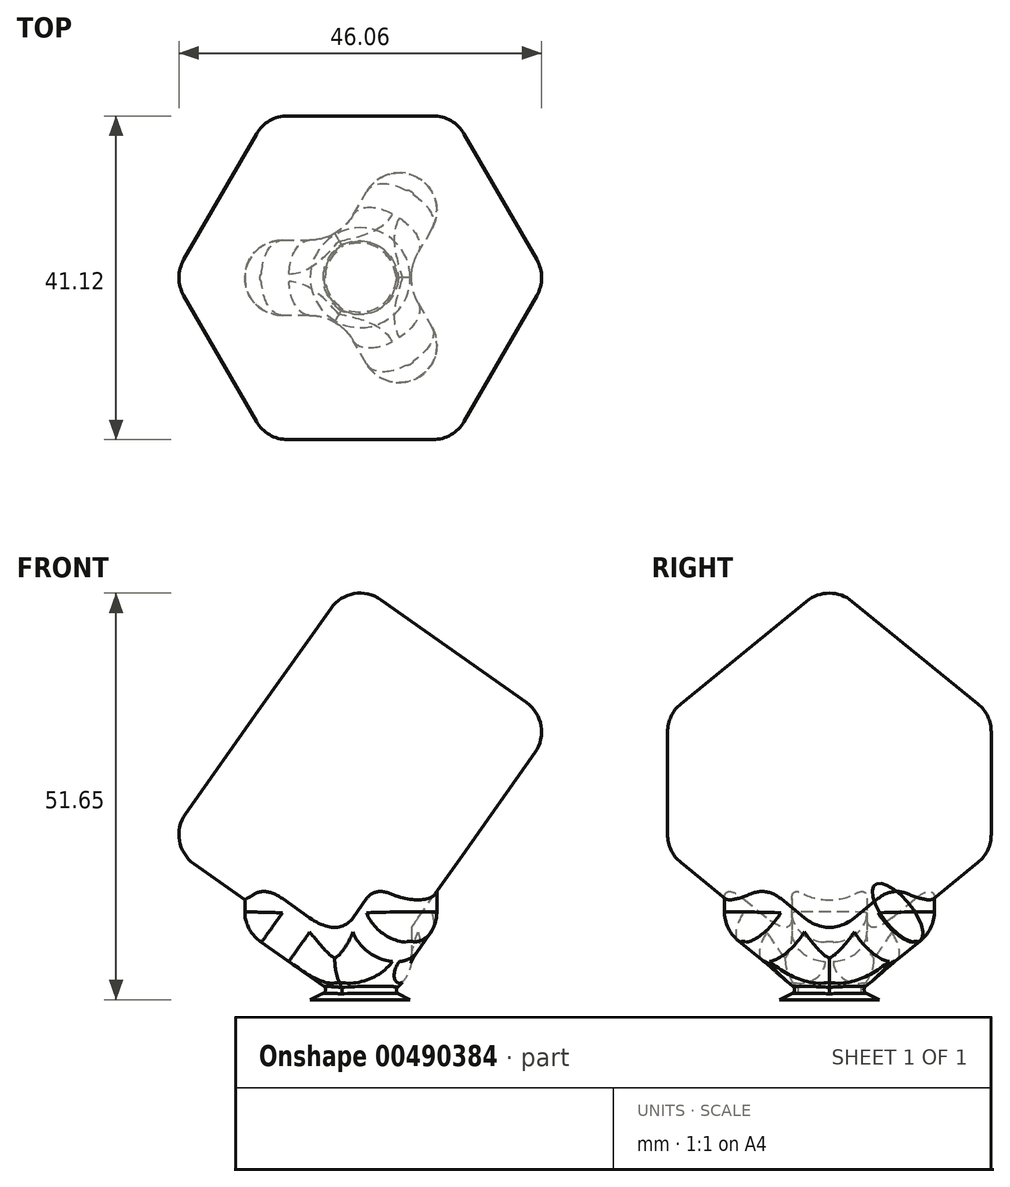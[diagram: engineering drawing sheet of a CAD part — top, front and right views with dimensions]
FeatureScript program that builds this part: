
annotation { "Feature Type Name" : "Feature", "Feature Type Description" : "" }
export const myFeature = defineFeature(function(context is Context, id is Id, definition is map)
    precondition{}
    {
        {
            var Q0;
            Q0=qCreatedBy(makeId("Front.planeOp"),FACE);
            var sketch = newSketch(context, id + "F0", { "sketchPlane" : qUnion([Q0])});
            skLineSegment(sketch, "E0", {"start": v(0, 0) * mm, "end": v(-25.92, 18.33) * mm});
            skLineSegment(sketch, "E1", {"start": v(-25.92, 18.33) * mm, "end": v(0, 55) * mm});
            skLineSegment(sketch, "E2", {"start": v(0, 55) * mm, "end": v(25.92, 36.66) * mm});
            skLineSegment(sketch, "E3", {"start": v(25.92, 36.66) * mm, "end": v(0, 0) * mm});
            skSolve(sketch);
        }
        {
            var Q0;
            Q0=sQuery(id+"F0.wireOp",EDGE,"E3");
            cPlane(context, id + "F1", {"entities" : qUnion([Q0]), "cplaneType" : CPlaneType.LINE_ANGLE, "offset" : 25.4 * mm, "angle" : 0 * degree, "width" : 152.4 * mm, "height" : 152.4 * mm});
        }
        {
            var Q0;
            Q0=qCreatedBy(id+"F1.planeOp",FACE);
            var sketch = newSketch(context, id + "F2", { "sketchPlane" : qUnion([Q0])});
            skLineSegment(sketch, "E4", {"start": v(0, 0) * mm, "end": v(-22.45, 22.45) * mm});
            skLineSegment(sketch, "E5", {"start": v(-22.45, 22.45) * mm, "end": v(0, 44.9) * mm});
            skLineSegment(sketch, "E6", {"start": v(0, 44.9) * mm, "end": v(22.45, 22.45) * mm});
            skLineSegment(sketch, "E7", {"start": v(22.45, 22.45) * mm, "end": v(0, 0) * mm});
            skSolve(sketch);
        }
        {
            var Q0;
            Q0 = qSketchRegion(id + "F2", true);
            extrude(context, id + "F3", {"entities" : qUnion([Q0]), "depth" : 31.75 * mm});
        }
        {
            var Q0;
            Q0=makeQuery(id+"F3.opExtrude","SWEPT_FACE",FACE,{"disambiguationData":[OSD([sQuery(id+"F2.wireOp",EDGE,"E7")])]});
            var Q1;
            Q1=makeQuery(id+"F3.opExtrude","SWEPT_FACE",FACE,{"disambiguationData":[OSD([sQuery(id+"F2.wireOp",EDGE,"E6")])]});
            var Q2;
            Q2=makeQuery(id+"F3.opExtrude","CAP_FACE",FACE,{"disambiguationData":[OSD([sQuery(id+"F2.wireOp",EDGE,"E4"),sQuery(id+"F2.wireOp",EDGE,"E5"),sQuery(id+"F2.wireOp",EDGE,"E6"),sQuery(id+"F2.wireOp",EDGE,"E7")])],"isStart":true});
            var Q3;
            Q3=makeQuery(id+"F3.opExtrude","SWEPT_FACE",FACE,{"disambiguationData":[OSD([sQuery(id+"F2.wireOp",EDGE,"E5")])]});
            var Q4;
            Q4=makeQuery(id+"F3.opExtrude","CAP_FACE",FACE,{"disambiguationData":[OSD([sQuery(id+"F2.wireOp",EDGE,"E4"),sQuery(id+"F2.wireOp",EDGE,"E5"),sQuery(id+"F2.wireOp",EDGE,"E6"),sQuery(id+"F2.wireOp",EDGE,"E7")])],"isStart":false});
            var Q5;
            Q5=makeQuery(id+"F3.opExtrude","SWEPT_FACE",FACE,{"disambiguationData":[OSD([sQuery(id+"F2.wireOp",EDGE,"E4")])]});
            fillet(context, id + "F4", {"entities" : qUnion([Q0, Q1, Q2, Q3, Q4, Q5]), "radius" : 4.57 * mm, "tangentPropagation" : true, "allowEdgeOverflow" : false});
        }
        {
            var Q0;
            Q0=qCreatedBy(makeId("Top.planeOp"),FACE);
            var sketch = newSketch(context, id + "F5", { "sketchPlane" : qUnion([Q0])});
            skLineSegment(sketch, "E8", {"start": v(0, 0) * mm, "end": v(7.33, -12.7) * mm, "construction": true});
            skLineSegment(sketch, "E9", {"start": v(7.33, -12.7) * mm, "end": v(7.33, 12.7) * mm, "construction": true});
            skLineSegment(sketch, "E10", {"start": v(7.33, 12.7) * mm, "end": v(0, 0) * mm, "construction": true});
            skLineSegment(sketch, "E11", {"start": v(9.08, -6.18) * mm, "end": v(7.35, -3.18) * mm, "construction": true});
            skLineSegment(sketch, "E12", {"start": v(7.35, 3.17) * mm, "end": v(9.08, 6.18) * mm, "construction": true});
            skArc(sketch, "E13", {"start": v(7.33, -12.7) * mm, "mid": v(9.56, -9.8) * mm, "end": v(9.08, -6.18) * mm, "construction": true});
            skArc(sketch, "E14", {"start": v(9.08, 6.18) * mm, "mid": v(9.56, 9.8) * mm, "end": v(7.33, 12.7) * mm, "construction": true});
            skArc(sketch, "E15", {"start": v(7.35, 3.17) * mm, "mid": v(6.5, 0) * mm, "end": v(7.35, -3.17) * mm, "construction": true});
            skLineSegment(sketch, "E16", {"start": v(0, 0) * mm, "end": v(12.85, 0) * mm, "construction": true});
            skArc(sketch, "E17.1.0", {"start": v(7.33, 12.7) * mm, "mid": v(3.7, 13.18) * mm, "end": v(0.8, 10.95) * mm, "construction": true});
            skLineSegment(sketch, "E17.1.1", {"start": v(0.8, 10.95) * mm, "end": v(-0.92, 7.95) * mm, "construction": true});
            skArc(sketch, "E17.1.2", {"start": v(-6.42, 4.78) * mm, "mid": v(-4.78, 5) * mm, "end": v(-3.25, 5.63) * mm});
            skLineSegment(sketch, "E17.1.3", {"start": v(-6.42, 4.78) * mm, "end": v(-9.89, 4.78) * mm});
            skArc(sketch, "E17.1.4", {"start": v(-9.89, 4.78) * mm, "mid": v(-13.27, 3.38) * mm, "end": v(-14.66, 0) * mm});
            skArc(sketch, "E17.2.0", {"start": v(-14.66, 0) * mm, "mid": v(-13.27, -3.38) * mm, "end": v(-9.89, -4.78) * mm});
            skLineSegment(sketch, "E17.2.1", {"start": v(-9.89, -4.78) * mm, "end": v(-6.42, -4.78) * mm});
            skArc(sketch, "E17.2.2", {"start": v(-0.92, -7.95) * mm, "mid": v(-1.93, -6.64) * mm, "end": v(-3.25, -5.63) * mm});
            skLineSegment(sketch, "E17.2.3", {"start": v(-0.92, -7.95) * mm, "end": v(0.8, -10.95) * mm, "construction": true});
            skArc(sketch, "E17.2.4", {"start": v(0.8, -10.95) * mm, "mid": v(3.7, -13.18) * mm, "end": v(7.33, -12.7) * mm, "construction": true});
            skPoint(sketch, "E17.center", {"position": v(0, 0) * mm});
            skLineSegment(sketch, "E18", {"start": v(0, 0) * mm, "end": v(-3.25, 5.63) * mm});
            skLineSegment(sketch, "E19", {"start": v(0, 0) * mm, "end": v(-3.25, -5.63) * mm});
            skArc(sketch, "E20", {"start": v(-3.25, 5.63) * mm, "mid": v(-1.93, 6.64) * mm, "end": v(-0.92, 7.95) * mm});
            skArc(sketch, "E21", {"start": v(-3.25, -5.63) * mm, "mid": v(-4.78, -5) * mm, "end": v(-6.42, -4.78) * mm});
            skSolve(sketch);
        }
        {
            var Q0;
            Q0=makeQuery(id+"F5.imprint","IMPRINT",FACE,{"disambiguationData":[TD([[makeQuery(id+"F5.imprint","IMPRINT",EDGE,{"derivedFrom":sQuery(id+"F5.wireOp",EDGE,"E17.1.2")}),-1.0]])]});
            var Q1;
            Q1=makeQuery(id+"F3.opExtrude","SWEPT_BODY",BODY,{"disambiguationData":[OSD([sQuery(id+"F2.wireOp",EDGE,"E4"),sQuery(id+"F2.wireOp",EDGE,"E5"),sQuery(id+"F2.wireOp",EDGE,"E6"),sQuery(id+"F2.wireOp",EDGE,"E7")])]});
            extrude(context, id + "F6", {"entities" : qUnion([Q0]), "endBound" : BoundingType.UP_TO_BODY, "endBoundEntityBody" : qUnion([Q1]), "depth" : 25.4 * mm});
        }
        {
            var Q0;
            Q0=qCreatedBy(id+"F1.planeOp",FACE);
            var sketch = newSketch(context, id + "F7", { "sketchPlane" : qUnion([Q0])});
            skArc(sketch, "E22", {"start": v(-5.63, 1.14) * mm, "mid": v(0, -1.28) * mm, "end": v(5.63, 1.14) * mm});
            skLineSegment(sketch, "E23", {"start": v(15.4, -11.7) * mm, "end": v(-17.38, -11.7) * mm});
            skLineSegment(sketch, "E24", {"start": v(-17.38, 1.14) * mm, "end": v(-17.38, -11.7) * mm});
            skLineSegment(sketch, "E25", {"start": v(15.4, 1.14) * mm, "end": v(15.4, -11.7) * mm});
            skLineSegment(sketch, "E26", {"start": v(-5.63, 1.14) * mm, "end": v(-17.38, 1.14) * mm});
            skLineSegment(sketch, "E27", {"start": v(5.63, 1.14) * mm, "end": v(15.4, 1.14) * mm});
            skSolve(sketch);
        }
        {
            var Q0;
            Q0 = qSketchRegion(id + "F7", true);
            extrude(context, id + "F8", {"entities" : qUnion([Q0]), "operationType" : NewBodyOperationType.REMOVE, "endBound" : BoundingType.THROUGH_ALL, "depth" : 25.4 * mm, "hasSecondDirection" : true, "secondDirectionBound" : SecondDirectionBoundingType.THROUGH_ALL, "secondDirectionOppositeDirection" : true, "secondDirectionDepth" : 25.4 * mm});
        }
        {
            var Q0;
            Q0=makeQuery(id+"F6.opExtrude","SWEPT_BODY",BODY,{"disambiguationData":[OSD([sQuery(id+"F5.wireOp",EDGE,"E17.1.2"),sQuery(id+"F5.wireOp",EDGE,"E17.1.3"),sQuery(id+"F5.wireOp",EDGE,"E17.1.4"),sQuery(id+"F5.wireOp",EDGE,"E17.2.0"),sQuery(id+"F5.wireOp",EDGE,"E17.2.1"),sQuery(id+"F5.wireOp",EDGE,"E18"),sQuery(id+"F5.wireOp",EDGE,"E19"),sQuery(id+"F5.wireOp",EDGE,"E21")])]});
            var Q1;
            Q1=makeQuery(id+"F6.opExtrude","SWEPT_EDGE",EDGE,{"disambiguationData":[OSD([sQuery(id+"F5.wireOp",EDGE,"E18"),sQuery(id+"F5.wireOp",EDGE,"E19")])]});
            circularPattern(context, id + "F9", {"operationType" : NewBodyOperationType.ADD, "entities" : qUnion([Q0]), "axis" : qUnion([Q1]), "angle" : 360 * degree, "instanceCount" : 3, "equalSpace" : true});
        }
        {
            var Q0;
            Q0=qCreatedBy(makeId("Front.planeOp"),FACE);
            var sketch = newSketch(context, id + "F10", { "sketchPlane" : qUnion([Q0])});
            skLineSegment(sketch, "E28", {"start": v(0, 3.18) * mm, "end": v(6.35, 0) * mm});
            skPoint(sketch, "E29.orphan", {"position": v(6.5, 3.7) * mm});
            skLineSegment(sketch, "E30", {"start": v(0, 0) * mm, "end": v(0, 3.18) * mm});
            skLineSegment(sketch, "E31", {"start": v(6.35, 0) * mm, "end": v(0, 0) * mm});
            skSolve(sketch);
        }
        {
            var Q0;
            Q0=makeQuery(id+"F10.imprint","IMPRINT",FACE,{"disambiguationData":[TD([[makeQuery(id+"F10.imprint","IMPRINT",EDGE,{"derivedFrom":sQuery(id+"F10.wireOp",EDGE,"E28")}),-1.0]])]});
            var Q1;
            Q1=sQuery(id+"F10.wireOp",EDGE,"E30");
            revolve(context, id + "F11", {"operationType" : NewBodyOperationType.ADD, "entities" : qUnion([Q0]), "axis" : qUnion([Q1]), "revolveType" : RevolveType.FULL});
        }
        {
            var Q0;
            Q0=makeQuery(id+"F11.boolean.opBoolean","INTERSECT",EDGE,{"derivedFrom":[makeQuery(id+"F9.opPattern","COPY",FACE,{"derivedFrom":makeQuery(id+"F8.boolean.opBoolean","COPY",FACE,{"derivedFrom":makeQuery(id+"F8.opExtrude","SWEPT_FACE",FACE,{"disambiguationData":[OSD([sQuery(id+"F7.wireOp",EDGE,"E22")])]})}),"instanceName":"2"}),makeQuery(id+"F11.opRevolve","SWEPT_FACE",FACE,{"disambiguationData":[OSD([sQuery(id+"F10.wireOp",EDGE,"E28")])]})]});
            var Q1;
            Q1=makeQuery(id+"F11.boolean.opBoolean","INTERSECT",EDGE,{"derivedFrom":[makeQuery(id+"F8.boolean.opBoolean","COPY",FACE,{"derivedFrom":makeQuery(id+"F8.opExtrude","SWEPT_FACE",FACE,{"disambiguationData":[OSD([sQuery(id+"F7.wireOp",EDGE,"E22")])]})}),makeQuery(id+"F11.opRevolve","SWEPT_FACE",FACE,{"disambiguationData":[OSD([sQuery(id+"F10.wireOp",EDGE,"E28")])]})]});
            var Q2;
            Q2=makeQuery(id+"F11.boolean.opBoolean","INTERSECT",EDGE,{"derivedFrom":[makeQuery(id+"F9.opPattern","COPY",FACE,{"derivedFrom":makeQuery(id+"F8.boolean.opBoolean","COPY",FACE,{"derivedFrom":makeQuery(id+"F8.opExtrude","SWEPT_FACE",FACE,{"disambiguationData":[OSD([sQuery(id+"F7.wireOp",EDGE,"E22")])]})}),"instanceName":"1"}),makeQuery(id+"F11.opRevolve","SWEPT_FACE",FACE,{"disambiguationData":[OSD([sQuery(id+"F10.wireOp",EDGE,"E28")])]})]});
            fillet(context, id + "F12", {"entities" : qUnion([Q0, Q1, Q2]), "radius" : 0.5 * mm, "tangentPropagation" : true, "allowEdgeOverflow" : false});
        }
        {
            var Q0;
            Q0=makeQuery(id+"F9.opPattern","COPY",EDGE,{"derivedFrom":makeQuery(id+"F8.boolean.opBoolean","INTERSECT",EDGE,{"derivedFrom":[makeQuery(id+"F6.opExtrude","SWEPT_FACE",FACE,{"disambiguationData":[OSD([sQuery(id+"F5.wireOp",EDGE,"E17.1.3")])]}),makeQuery(id+"F8.opExtrude","SWEPT_FACE",FACE,{"disambiguationData":[OSD([sQuery(id+"F7.wireOp",EDGE,"E22")])]})]}),"instanceName":"2"});
            var Q1;
            Q1=makeQuery(id+"F8.boolean.opBoolean","INTERSECT",EDGE,{"derivedFrom":[makeQuery(id+"F6.opExtrude","SWEPT_FACE",FACE,{"disambiguationData":[OSD([sQuery(id+"F5.wireOp",EDGE,"E21")])]}),makeQuery(id+"F8.opExtrude","SWEPT_FACE",FACE,{"disambiguationData":[OSD([sQuery(id+"F7.wireOp",EDGE,"E22")])]})]});
            var Q2;
            Q2=makeQuery(id+"F9.opPattern","COPY",EDGE,{"derivedFrom":makeQuery(id+"F8.boolean.opBoolean","INTERSECT",EDGE,{"derivedFrom":[makeQuery(id+"F6.opExtrude","SWEPT_FACE",FACE,{"disambiguationData":[OSD([sQuery(id+"F5.wireOp",EDGE,"E21")])]}),makeQuery(id+"F8.opExtrude","SWEPT_FACE",FACE,{"disambiguationData":[OSD([sQuery(id+"F7.wireOp",EDGE,"E22")])]})]}),"instanceName":"1"});
            fillet(context, id + "F13", {"entities" : qUnion([Q0, Q1, Q2]), "radius" : 4.57 * mm, "tangentPropagation" : true, "allowEdgeOverflow" : false});
        }
    });
